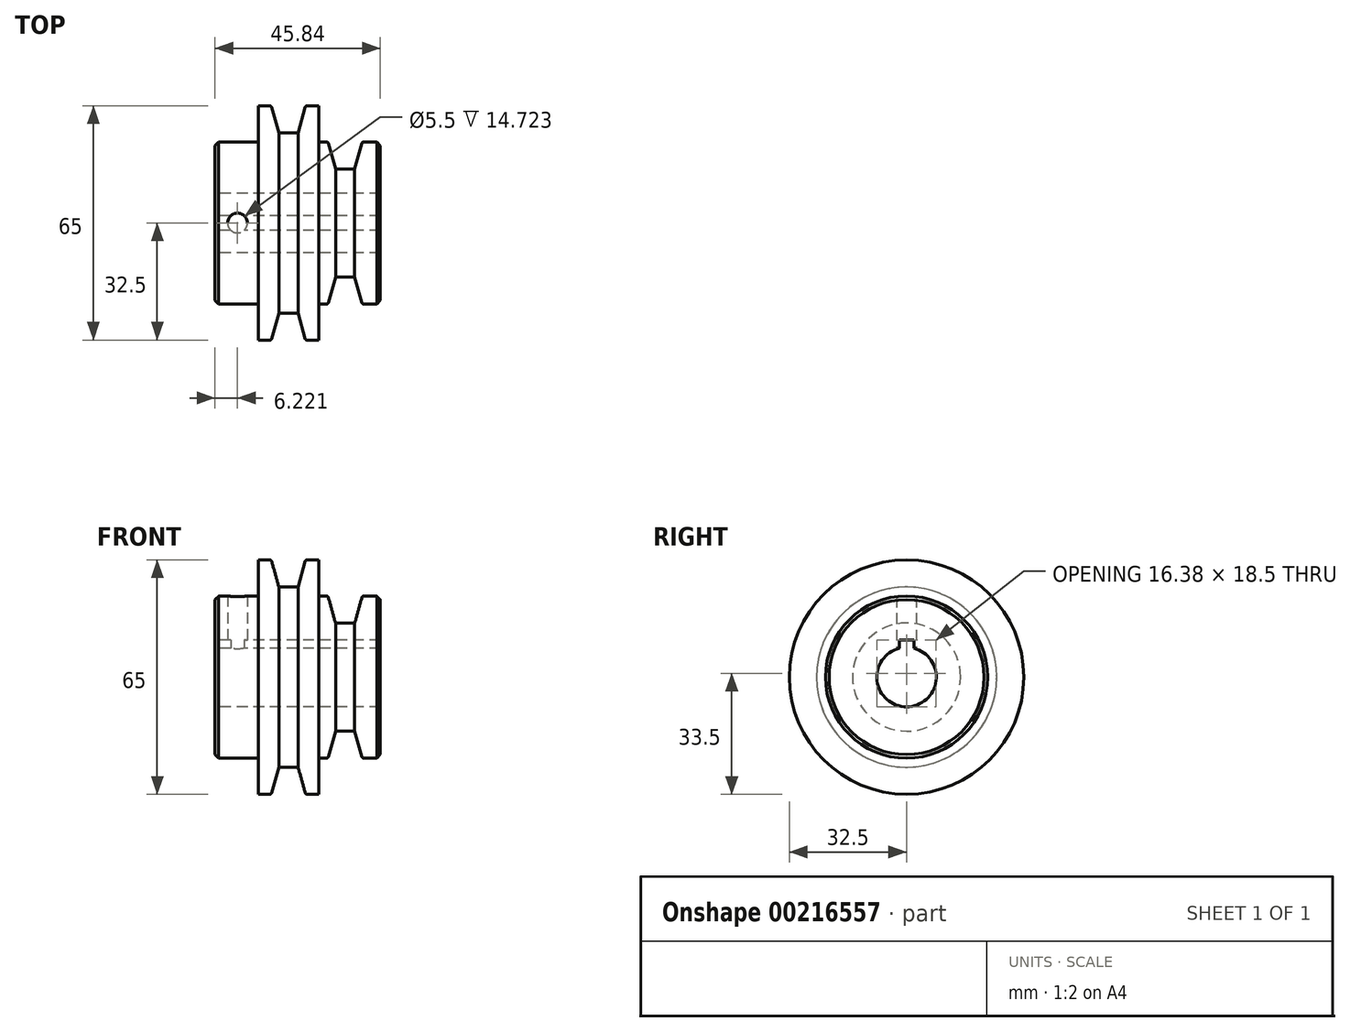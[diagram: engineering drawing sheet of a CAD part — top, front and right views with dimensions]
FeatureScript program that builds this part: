
annotation { "Feature Type Name" : "Feature", "Feature Type Description" : "" }
export const myFeature = defineFeature(function(context is Context, id is Id, definition is map)
    precondition{}
    {
        {
            var Q0;
            Q0=qCreatedBy(makeId("Front.planeOp"),FACE);
            var sketch = newSketch(context, id + "F0", { "sketchPlane" : qUnion([Q0])});
            skLineSegment(sketch, "E0", {"start": v(-137.98, 0) * mm, "end": v(156, 0) * mm, "construction": true});
            skLineSegment(sketch, "E1.bottom", {"start": v(-16.36, 8.25) * mm, "end": v(0.36, 8.25) * mm});
            skLineSegment(sketch, "E1.top", {"start": v(-16.36, 32.5) * mm, "end": v(-12.76, 32.5) * mm});
            skLineSegment(sketch, "E1.left", {"start": v(-16.36, 22.5) * mm, "end": v(-16.36, 32.5) * mm});
            skLineSegment(sketch, "E2.bottom", {"start": v(0.36, 8.25) * mm, "end": v(17.48, 8.25) * mm});
            skLineSegment(sketch, "E2.right", {"start": v(17.48, 8.25) * mm, "end": v(17.48, 22.5) * mm});
            skLineSegment(sketch, "E3", {"start": v(-3.24, 32.5) * mm, "end": v(-5.33, 25) * mm});
            skLineSegment(sketch, "E4", {"start": v(-5.33, 25) * mm, "end": v(-10.67, 25) * mm});
            skLineSegment(sketch, "E5", {"start": v(-10.67, 25) * mm, "end": v(-12.76, 32.5) * mm});
            skLineSegment(sketch, "E6.trimOffspring", {"start": v(-3.24, 32.5) * mm, "end": v(0.36, 32.5) * mm});
            skLineSegment(sketch, "E7.trimOffspring", {"start": v(12.48, 22.5) * mm, "end": v(17.48, 22.5) * mm});
            skLineSegment(sketch, "E8", {"start": v(-8, 39.04) * mm, "end": v(-8, 0) * mm, "construction": true});
            skPoint(sketch, "E9.start.orphan", {"position": v(0, 21.9) * mm});
            skLineSegment(sketch, "E10", {"start": v(2.96, 22.5) * mm, "end": v(5.05, 15) * mm});
            skLineSegment(sketch, "E11", {"start": v(5.05, 15) * mm, "end": v(10.39, 15) * mm});
            skLineSegment(sketch, "E12", {"start": v(10.39, 15) * mm, "end": v(12.48, 22.5) * mm});
            skLineSegment(sketch, "E13.bottom", {"start": v(-16.36, 8.25) * mm, "end": v(-28.36, 8.25) * mm});
            skLineSegment(sketch, "E13.top", {"start": v(-16.36, 22.5) * mm, "end": v(-28.36, 22.5) * mm});
            skLineSegment(sketch, "E13.right", {"start": v(-28.36, 8.25) * mm, "end": v(-28.36, 22.5) * mm});
            skPoint(sketch, "E14.end.orphan", {"position": v(2.96, 22.5) * mm});
            skLineSegment(sketch, "E15", {"start": v(0.36, 32.5) * mm, "end": v(0.36, 22.5) * mm});
            skLineSegment(sketch, "E16", {"start": v(0.36, 22.5) * mm, "end": v(2.96, 22.5) * mm});
            skSolve(sketch);
        }
        {
            var Q0;
            Q0 = qSketchRegion(id + "F0", true);
            var Q1;
            Q1=sQuery(id+"F0.wireOp",EDGE,"E0");
            revolve(context, id + "F1", {"entities" : qUnion([Q0]), "axis" : qUnion([Q1]), "revolveType" : RevolveType.FULL});
        }
        {
            var Q0;
            Q0=makeQuery(id+"F1.opRevolve","SWEPT_EDGE",EDGE,{"disambiguationData":[OSD([sQuery(id+"F0.wireOp",EDGE,"E13.top"),sQuery(id+"F0.wireOp",EDGE,"E13.right")])]});
            var Q1;
            Q1=makeQuery(id+"F1.opRevolve","SWEPT_EDGE",EDGE,{"disambiguationData":[OSD([sQuery(id+"F0.wireOp",EDGE,"E2.right"),sQuery(id+"F0.wireOp",EDGE,"E7.trimOffspring")])]});
            chamfer(context, id + "F2", {"entities" : qUnion([Q0, Q1]), "width" : 1 * mm, "tangentPropagation" : true});
        }
        {
            var Q0;
            Q0=makeQuery(id+"F1.opRevolve","SWEPT_EDGE",EDGE,{"disambiguationData":[OSD([sQuery(id+"F0.wireOp",EDGE,"E1.top"),sQuery(id+"F0.wireOp",EDGE,"E5")])]});
            var Q1;
            Q1=makeQuery(id+"F1.opRevolve","SWEPT_EDGE",EDGE,{"disambiguationData":[OSD([sQuery(id+"F0.wireOp",EDGE,"E3"),sQuery(id+"F0.wireOp",EDGE,"E6.trimOffspring")])]});
            var Q2;
            Q2=makeQuery(id+"F1.opRevolve","SWEPT_EDGE",EDGE,{"disambiguationData":[OSD([sQuery(id+"F0.wireOp",EDGE,"E10"),sQuery(id+"F0.wireOp",EDGE,"E16")])]});
            var Q3;
            Q3=makeQuery(id+"F1.opRevolve","SWEPT_EDGE",EDGE,{"disambiguationData":[OSD([sQuery(id+"F0.wireOp",EDGE,"E7.trimOffspring"),sQuery(id+"F0.wireOp",EDGE,"E12")])]});
            fillet(context, id + "F3", {"entities" : qUnion([Q0, Q1, Q2, Q3]), "radius" : .5 * mm, "tangentPropagation" : true, "allowEdgeOverflow" : false});
        }
        {
            var Q0;
            Q0=makeQuery(id+"F1.opRevolve","SWEPT_FACE",FACE,{"disambiguationData":[OSD([sQuery(id+"F0.wireOp",EDGE,"E13.right")])]});
            var sketch = newSketch(context, id + "F4", { "sketchPlane" : qUnion([Q0])});
            skLineSegment(sketch, "E17", {"start": v(0, 0) * mm, "end": v(0, 17.88) * mm, "construction": true});
            skLineSegment(sketch, "E18.bottom", {"start": v(-2, 6.25) * mm, "end": v(2, 6.25) * mm});
            skLineSegment(sketch, "E18.top", {"start": v(-2, 10.25) * mm, "end": v(2, 10.25) * mm});
            skLineSegment(sketch, "E18.left", {"start": v(-2, 6.25) * mm, "end": v(-2, 10.25) * mm});
            skLineSegment(sketch, "E18.right", {"start": v(2, 6.25) * mm, "end": v(2, 10.25) * mm});
            skPoint(sketch, "E18.middle", {"position": v(0, 8.25) * mm});
            skSolve(sketch);
        }
        {
            var Q0;
            Q0 = qSketchRegion(id + "F4", true);
            extrude(context, id + "F5", {"entities" : qUnion([Q0]), "operationType" : NewBodyOperationType.REMOVE, "endBound" : BoundingType.THROUGH_ALL, "oppositeDirection" : true, "depth" : 25 * mm});
        }
        {
            var Q0;
            Q0=qCreatedBy(makeId("Top.planeOp"),FACE);
            var sketch = newSketch(context, id + "F6", { "sketchPlane" : qUnion([Q0])});
            skCircle(sketch, "E19", {"center": v(-22.14, 0) * mm, "radius": 2.75 * mm});
            skSolve(sketch);
        }
        {
            var Q0;
            Q0 = qSketchRegion(id + "F6", true);
            extrude(context, id + "F7", {"entities" : qUnion([Q0]), "operationType" : NewBodyOperationType.REMOVE, "depth" : 25 * mm});
        }
    });
